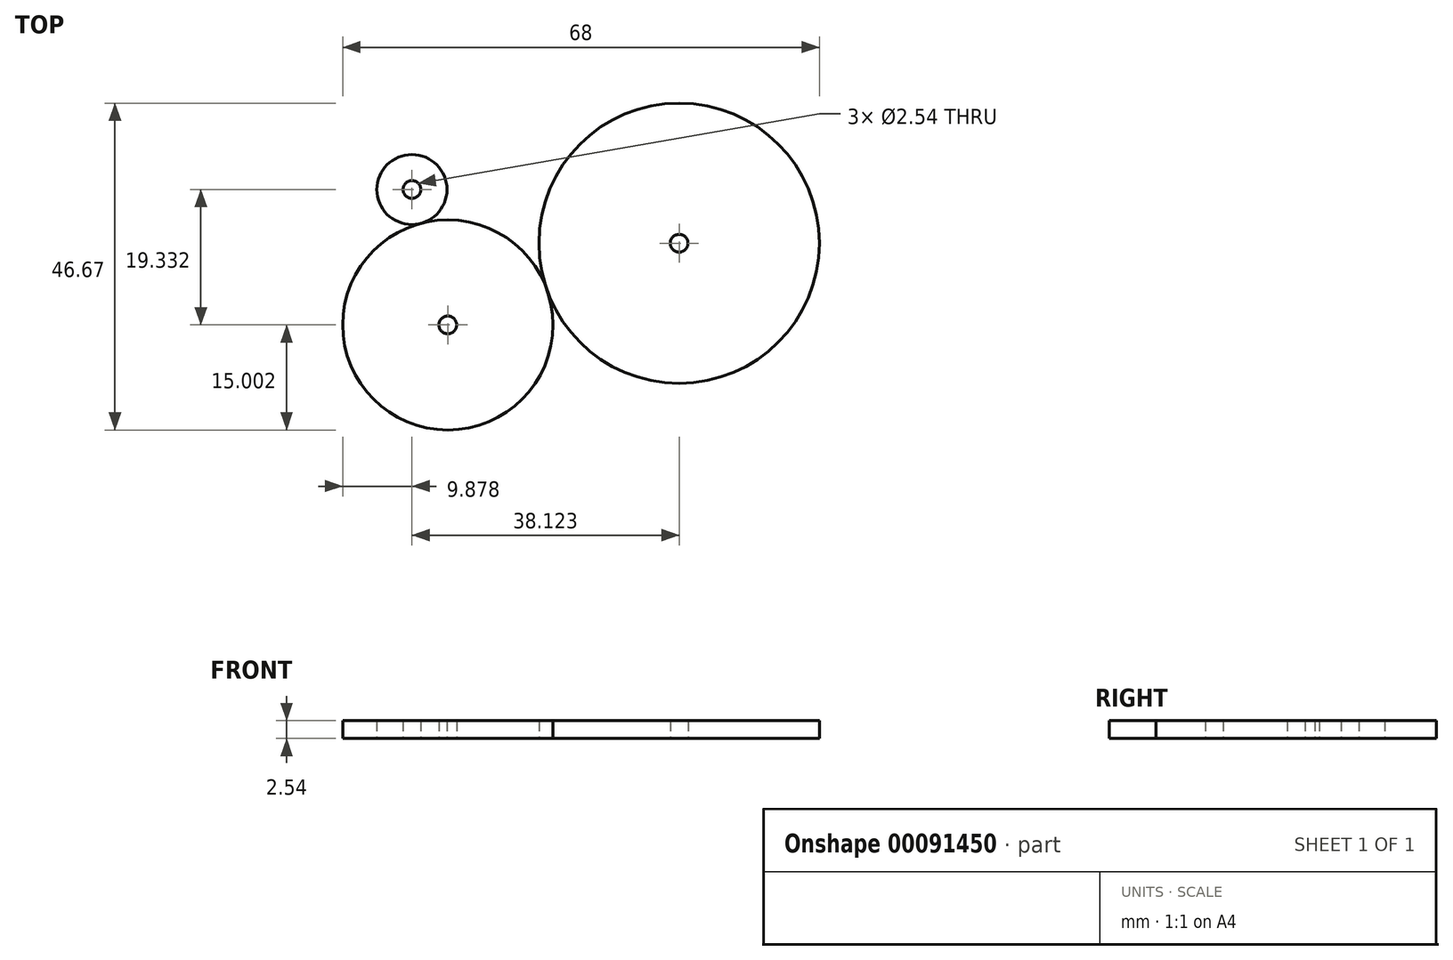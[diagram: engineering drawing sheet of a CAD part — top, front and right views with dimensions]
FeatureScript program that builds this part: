
annotation { "Feature Type Name" : "Feature", "Feature Type Description" : "" }
export const myFeature = defineFeature(function(context is Context, id is Id, definition is map)
    precondition{}
    {
        {
            var Q0;
            Q0=qCreatedBy(makeId("Top.planeOp"),FACE);
            var sketch = newSketch(context, id + "F0", { "sketchPlane" : qUnion([Q0])});
            skCircle(sketch, "E0", {"center": v(-20.19, -11.77) * mm, "radius": 15 * mm});
            skCircle(sketch, "E1", {"center": v(-25.31, 7.56) * mm, "radius": 5 * mm});
            skCircle(sketch, "E2", {"center": v(12.81, -0.1) * mm, "radius": 20 * mm});
            skCircle(sketch, "E3", {"center": v(-20.19, -11.77) * mm, "radius": 1.27 * mm});
            skCircle(sketch, "E4", {"center": v(-25.31, 7.56) * mm, "radius": 1.27 * mm});
            skCircle(sketch, "E5", {"center": v(12.81, -0.1) * mm, "radius": 1.27 * mm});
            skSolve(sketch);
        }
        {
            var Q0;
            Q0=makeQuery(id+"F0.imprint","IMPRINT",FACE,{"disambiguationData":[TD([[makeQuery(id+"F0.imprint","IMPRINT",EDGE,{"derivedFrom":sQuery(id+"F0.wireOp",EDGE,"E1")}),1.0]])]});
            var Q1;
            {var subQ0=sQuery(id+"F0.wireOp",EDGE,"E0");var subQ1=makeQuery(id+"F0.imprint","INTERSECT",VERTEX,{"derivedFrom":[subQ0,sQuery(id+"F0.wireOp",EDGE,"E1")]});Q1=makeQuery(id+"F0.imprint","IMPRINT",FACE,{"disambiguationData":[TD([[makeQuery(id+"F0.imprint","IMPRINT",EDGE,{"disambiguationData":[TD([[subQ1,1.0]])],"derivedFrom":subQ0}),1.0]])]});}
            var Q2;
            Q2=makeQuery(id+"F0.imprint","IMPRINT",FACE,{"disambiguationData":[TD([[makeQuery(id+"F0.imprint","IMPRINT",EDGE,{"derivedFrom":sQuery(id+"F0.wireOp",EDGE,"E2")}),1.0]])]});
            extrude(context, id + "F1", {"entities" : qUnion([Q0, Q1, Q2]), "depth" : 2.54 * mm});
        }
    });
